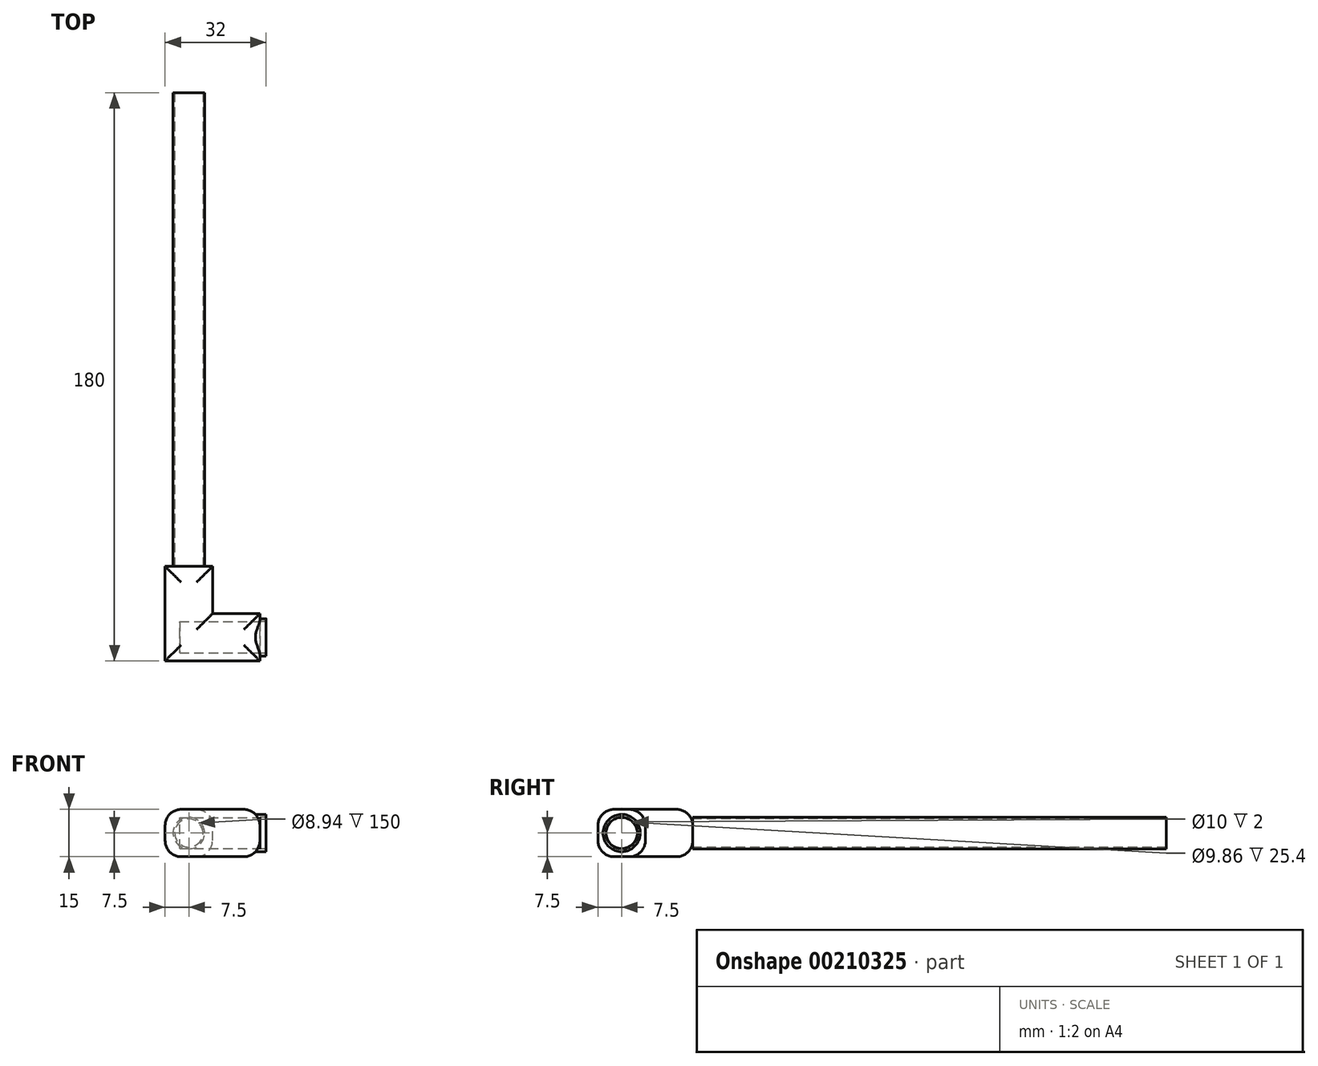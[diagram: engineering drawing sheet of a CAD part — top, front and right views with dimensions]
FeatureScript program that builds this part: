
annotation { "Feature Type Name" : "Feature", "Feature Type Description" : "" }
export const myFeature = defineFeature(function(context is Context, id is Id, definition is map)
    precondition{}
    {
        {
            var Q0;
            Q0=qCreatedBy(makeId("Front.planeOp"),FACE);
            var sketch = newSketch(context, id + "F0", { "sketchPlane" : qUnion([Q0])});
            skLineSegment(sketch, "E0.bottom", {"start": v(7.5, -7.5) * mm, "end": v(-7.5, -7.5) * mm});
            skLineSegment(sketch, "E0.top", {"start": v(7.5, 7.5) * mm, "end": v(-7.5, 7.5) * mm});
            skLineSegment(sketch, "E0.left", {"start": v(7.5, -7.5) * mm, "end": v(7.5, 7.5) * mm});
            skLineSegment(sketch, "E0.right", {"start": v(-7.5, -7.5) * mm, "end": v(-7.5, 7.5) * mm});
            skPoint(sketch, "E0.middle", {"position": v(0, 0) * mm});
            skLineSegment(sketch, "E1.bottom", {"start": v(5, -5) * mm, "end": v(-5, -5) * mm});
            skLineSegment(sketch, "E1.top", {"start": v(5, 5) * mm, "end": v(-5, 5) * mm});
            skLineSegment(sketch, "E1.left", {"start": v(5, -5) * mm, "end": v(5, 5) * mm});
            skLineSegment(sketch, "E1.right", {"start": v(-5, -5) * mm, "end": v(-5, 5) * mm});
            skSolve(sketch);
        }
        {
            var Q0;
            Q0=makeQuery(id+"F0.imprint","IMPRINT",FACE,{"disambiguationData":[TD([[makeQuery(id+"F0.imprint","IMPRINT",EDGE,{"derivedFrom":sQuery(id+"F0.wireOp",EDGE,"E0.bottom")}),-1.0]])]});
            extrude(context, id + "F1", {"entities" : qUnion([Q0]), "depth" : 30 * mm});
        }
        {
            var Q0;
            Q0=makeQuery(id+"F1.opExtrude","SWEPT_FACE",FACE,{"disambiguationData":[OSD([sQuery(id+"F0.wireOp",EDGE,"E0.left")])]});
            var sketch = newSketch(context, id + "F2", { "sketchPlane" : qUnion([Q0])});
            skLineSegment(sketch, "E2.bottom", {"start": v(-15, -7.5) * mm, "end": v(-30, -7.5) * mm});
            skLineSegment(sketch, "E2.top", {"start": v(-15, 7.5) * mm, "end": v(-30, 7.5) * mm});
            skLineSegment(sketch, "E2.left", {"start": v(-15, -7.5) * mm, "end": v(-15, 7.5) * mm});
            skLineSegment(sketch, "E2.right", {"start": v(-30, -7.5) * mm, "end": v(-30, 7.5) * mm});
            skPoint(sketch, "E2.middle", {"position": v(-22.5, 0) * mm});
            skLineSegment(sketch, "E3.bottom", {"start": v(-17.5, -5) * mm, "end": v(-27.5, -5) * mm});
            skLineSegment(sketch, "E3.top", {"start": v(-17.5, 5) * mm, "end": v(-27.5, 5) * mm});
            skLineSegment(sketch, "E3.left", {"start": v(-17.5, -5) * mm, "end": v(-17.5, 5) * mm});
            skLineSegment(sketch, "E3.right", {"start": v(-27.5, -5) * mm, "end": v(-27.5, 5) * mm});
            skSolve(sketch);
        }
        {
            var Q0;
            Q0=makeQuery(id+"F1.opExtrude","CAP_FACE",FACE,{"disambiguationData":[OSD([sQuery(id+"F0.wireOp",EDGE,"E0.bottom"),sQuery(id+"F0.wireOp",EDGE,"E0.top"),sQuery(id+"F0.wireOp",EDGE,"E0.left"),sQuery(id+"F0.wireOp",EDGE,"E0.right"),sQuery(id+"F0.wireOp",EDGE,"E1.bottom"),sQuery(id+"F0.wireOp",EDGE,"E1.top"),sQuery(id+"F0.wireOp",EDGE,"E1.left"),sQuery(id+"F0.wireOp",EDGE,"E1.right")])],"isStart":false});
            var sketch = newSketch(context, id + "F3", { "sketchPlane" : qUnion([Q0])});
            skLineSegment(sketch, "E4.bottom", {"start": v(5, 5) * mm, "end": v(-5, 5) * mm});
            skLineSegment(sketch, "E4.top", {"start": v(5, -5) * mm, "end": v(-5, -5) * mm});
            skLineSegment(sketch, "E4.left", {"start": v(5, 5) * mm, "end": v(5, -5) * mm});
            skLineSegment(sketch, "E4.right", {"start": v(-5, 5) * mm, "end": v(-5, -5) * mm});
            skSolve(sketch);
        }
        {
            var Q0;
            Q0=makeQuery(id+"F2.imprint","IMPRINT",FACE,{"disambiguationData":[TD([[makeQuery(id+"F2.imprint","IMPRINT",EDGE,{"derivedFrom":sQuery(id+"F2.wireOp",EDGE,"E2.bottom")}),1.0]])]});
            extrude(context, id + "F4", {"entities" : qUnion([Q0]), "operationType" : NewBodyOperationType.ADD, "depth" : 15 * mm});
        }
        {
            var Q0;
            Q0=makeQuery(id+"F3.imprint","IMPRINT",FACE,{"disambiguationData":[TD([[makeQuery(id+"F3.imprint","IMPRINT",EDGE,{"derivedFrom":sQuery(id+"F3.wireOp",EDGE,"E4.bottom")}),1.0]])]});
            extrude(context, id + "F5", {"entities" : qUnion([Q0]), "operationType" : NewBodyOperationType.ADD, "oppositeDirection" : true, "depth" : 30 * mm});
        }
        {
            var Q0;
            Q0=makeQuery(id+"F1.opExtrude","CAP_FACE",FACE,{"disambiguationData":[OSD([sQuery(id+"F0.wireOp",EDGE,"E0.bottom"),sQuery(id+"F0.wireOp",EDGE,"E0.top"),sQuery(id+"F0.wireOp",EDGE,"E0.left"),sQuery(id+"F0.wireOp",EDGE,"E0.right"),sQuery(id+"F0.wireOp",EDGE,"E1.bottom"),sQuery(id+"F0.wireOp",EDGE,"E1.top"),sQuery(id+"F0.wireOp",EDGE,"E1.left"),sQuery(id+"F0.wireOp",EDGE,"E1.right")])],"isStart":true});
            var sketch = newSketch(context, id + "F6", { "sketchPlane" : qUnion([Q0])});
            skCircle(sketch, "E5", {"center": v(0, 0) * mm, "radius": 5 * mm});
            skCircle(sketch, "E6", {"center": v(0, 0) * mm, "radius": 4.47 * mm});
            skSolve(sketch);
        }
        {
            var Q0;
            Q0=makeQuery(id+"F6.imprint","IMPRINT",FACE,{"disambiguationData":[TD([[makeQuery(id+"F6.imprint","IMPRINT",EDGE,{"derivedFrom":sQuery(id+"F6.wireOp",EDGE,"E6")}),-1.0]])]});
            extrude(context, id + "F7", {"entities" : qUnion([Q0]), "depth" : 150 * mm});
        }
        {
            var Q0;
            Q0=makeQuery(id+"F4.boolean.opBoolean","SPLIT",FACE,{"disambiguationData":[TD([makeQuery(id+"F4.opExtrude","SWEPT_FACE",FACE,{"disambiguationData":[OSD([sQuery(id+"F2.wireOp",EDGE,"E3.bottom")])]})])],"derivedFrom":makeQuery(id+"F1.opExtrude","SWEPT_FACE",FACE,{"disambiguationData":[OSD([sQuery(id+"F0.wireOp",EDGE,"E0.left")])]})});
            var sketch = newSketch(context, id + "F8", { "sketchPlane" : qUnion([Q0])});
            skLineSegment(sketch, "E7.bottom", {"start": v(-15, 7.5) * mm, "end": v(-30, 7.5) * mm});
            skLineSegment(sketch, "E7.top", {"start": v(-15, -7.5) * mm, "end": v(-30, -7.5) * mm});
            skLineSegment(sketch, "E7.left", {"start": v(-15, 7.5) * mm, "end": v(-15, -7.5) * mm});
            skLineSegment(sketch, "E7.right", {"start": v(-30, 7.5) * mm, "end": v(-30, -7.5) * mm});
            skPoint(sketch, "E7.middle", {"position": v(-22.5, 0) * mm});
            skLineSegment(sketch, "E8.bottom", {"start": v(-17.5, 5) * mm, "end": v(-27.5, 5) * mm});
            skLineSegment(sketch, "E8.top", {"start": v(-17.5, -5) * mm, "end": v(-27.5, -5) * mm});
            skLineSegment(sketch, "E8.left", {"start": v(-17.5, 5) * mm, "end": v(-17.5, -5) * mm});
            skLineSegment(sketch, "E8.right", {"start": v(-27.5, 5) * mm, "end": v(-27.5, -5) * mm});
            skSolve(sketch);
        }
        {
            var Q0;
            Q0=makeQuery(id+"F8.imprint","IMPRINT",FACE,{"disambiguationData":[TD([[makeQuery(id+"F8.imprint","IMPRINT",EDGE,{"derivedFrom":sQuery(id+"F8.wireOp",EDGE,"E8.bottom")}),1.0]])]});
            extrude(context, id + "F9", {"entities" : qUnion([Q0]), "operationType" : NewBodyOperationType.ADD, "depth" : 15 * mm});
        }
        {
            var Q0;
            Q0=makeQuery(id+"F9.boolean.opBoolean","MERGE",FACE,{"derivedFrom":[makeQuery(id+"F4.opExtrude","CAP_FACE",FACE,{"disambiguationData":[OSD([sQuery(id+"F2.wireOp",EDGE,"E2.bottom"),sQuery(id+"F2.wireOp",EDGE,"E2.top"),sQuery(id+"F2.wireOp",EDGE,"E2.left"),sQuery(id+"F2.wireOp",EDGE,"E2.right"),sQuery(id+"F2.wireOp",EDGE,"E3.bottom"),sQuery(id+"F2.wireOp",EDGE,"E3.top"),sQuery(id+"F2.wireOp",EDGE,"E3.left"),sQuery(id+"F2.wireOp",EDGE,"E3.right")])],"isStart":false}),makeQuery(id+"F9.opExtrude","CAP_FACE",FACE,{"disambiguationData":[OSD([sQuery(id+"F8.wireOp",EDGE,"E8.bottom"),sQuery(id+"F8.wireOp",EDGE,"E8.top"),sQuery(id+"F8.wireOp",EDGE,"E8.left"),sQuery(id+"F8.wireOp",EDGE,"E8.right")])],"isStart":false})]});
            var sketch = newSketch(context, id + "F10", { "sketchPlane" : qUnion([Q0])});
            skCircle(sketch, "E9", {"center": v(-22.5, 0) * mm, "radius": 5.9 * mm});
            skLineSegment(sketch, "E10", {"start": v(-15, -7.5) * mm, "end": v(-30, 7.5) * mm, "construction": true});
            skLineSegment(sketch, "E11", {"start": v(-30, 7.5) * mm, "end": v(-30, -7.5) * mm, "construction": true});
            skLineSegment(sketch, "E12", {"start": v(-30, -7.5) * mm, "end": v(-15, 7.5) * mm, "construction": true});
            skCircle(sketch, "E13", {"center": v(-22.5, 0) * mm, "radius": 5 * mm});
            skSolve(sketch);
        }
        {
            var Q0;
            Q0=makeQuery(id+"F10.imprint","IMPRINT",FACE,{"disambiguationData":[TD([[makeQuery(id+"F10.imprint","IMPRINT",EDGE,{"derivedFrom":sQuery(id+"F10.wireOp",EDGE,"E9")}),1.0]])]});
            extrude(context, id + "F11", {"entities" : qUnion([Q0]), "operationType" : NewBodyOperationType.ADD, "depth" : 2 * mm});
        }
        {
            var Q0;
            Q0=makeQuery(id+"F11.boolean.opBoolean","SPLIT",FACE,{"disambiguationData":[TD([makeQuery(id+"F11.opExtrude","SWEPT_FACE",FACE,{"disambiguationData":[OSD([sQuery(id+"F10.wireOp",EDGE,"E13")])]})])],"derivedFrom":makeQuery(id+"F9.boolean.opBoolean","MERGE",FACE,{"derivedFrom":[makeQuery(id+"F4.opExtrude","CAP_FACE",FACE,{"disambiguationData":[OSD([sQuery(id+"F2.wireOp",EDGE,"E2.bottom"),sQuery(id+"F2.wireOp",EDGE,"E2.top"),sQuery(id+"F2.wireOp",EDGE,"E2.left"),sQuery(id+"F2.wireOp",EDGE,"E2.right"),sQuery(id+"F2.wireOp",EDGE,"E3.bottom"),sQuery(id+"F2.wireOp",EDGE,"E3.top"),sQuery(id+"F2.wireOp",EDGE,"E3.left"),sQuery(id+"F2.wireOp",EDGE,"E3.right")])],"isStart":false}),makeQuery(id+"F9.opExtrude","CAP_FACE",FACE,{"disambiguationData":[OSD([sQuery(id+"F8.wireOp",EDGE,"E8.bottom"),sQuery(id+"F8.wireOp",EDGE,"E8.top"),sQuery(id+"F8.wireOp",EDGE,"E8.left"),sQuery(id+"F8.wireOp",EDGE,"E8.right")])],"isStart":false})]})});
            var sketch = newSketch(context, id + "F12", { "sketchPlane" : qUnion([Q0])});
            skCircle(sketch, "E14", {"center": v(-22.5, 0) * mm, "radius": 4.93 * mm});
            skSolve(sketch);
        }
        {
            var Q0;
            Q0=makeQuery(id+"F12.imprint","IMPRINT",FACE,{"disambiguationData":[TD([[makeQuery(id+"F12.imprint","IMPRINT",EDGE,{"derivedFrom":sQuery(id+"F12.wireOp",EDGE,"E14")}),1.0]])]});
            extrude(context, id + "F13", {"entities" : qUnion([Q0]), "operationType" : NewBodyOperationType.REMOVE, "oppositeDirection" : true, "depth" : 25.4 * mm});
        }
        {
            var Q0;
            Q0=makeQuery(id+"F4.boolean.opBoolean","MERGE",FACE,{"derivedFrom":[makeQuery(id+"F1.opExtrude","SWEPT_FACE",FACE,{"disambiguationData":[OSD([sQuery(id+"F0.wireOp",EDGE,"E0.top")])]}),makeQuery(id+"F4.opExtrude","SWEPT_FACE",FACE,{"disambiguationData":[OSD([sQuery(id+"F2.wireOp",EDGE,"E2.top")])]})]});
            var Q1;
            Q1=makeQuery(id+"F4.boolean.opBoolean","MERGE",FACE,{"derivedFrom":[makeQuery(id+"F1.opExtrude","SWEPT_FACE",FACE,{"disambiguationData":[OSD([sQuery(id+"F0.wireOp",EDGE,"E0.bottom")])]}),makeQuery(id+"F4.opExtrude","SWEPT_FACE",FACE,{"disambiguationData":[OSD([sQuery(id+"F2.wireOp",EDGE,"E2.bottom")])]})]});
            fillet(context, id + "F14", {"entities" : qUnion([Q0, Q1]), "radius" : 5.08 * mm, "tangentPropagation" : true, "allowEdgeOverflow" : false});
        }
    });
